FREECAD ASSEMBLY — COMPONENT RECIPES ("Assembly_LinkageUnit")

This assembly document has 6 components, labeled P0..P5 below (a component is one placed body or linked part). 6 of them carry a construction recipe — the FreeCAD feature program that regenerates the part from scratch, quoted from this document or its linked companion documents; the rest are supplied as boundary geometry only. No exploded tour is included for this assembly.
COMPONENT P0 — recipe-attached ("LinkageRod1", a linked part whose construction recipe lives in a companion FreeCAD document of the same project; that document's serialized recipe follows).
Construction recipe (the companion document, serialized — sketch geometry with constraints, then the solid features built on it; lengths are millimeters unless a unit is written):

FCSTD DOCUMENT  (FreeCAD 1.2R45145 (Git))
Label: LinkageRod
License: All rights reserved
LicenseURL: https://en.wikipedia.org/wiki/All_rights_reserved
objects: Sketcher::SketchObject×2, App::Point×1, PartDesign::Pad×1, PartDesign::Chamfer×1, PartDesign::Groove×1, PartDesign::Mirrored×1, PartDesign::Body×1
note: 16 computed .brp shape members not serialized (recipe doc carries the construction recipe); baked Part::Feature solids carry a one-line shape summary decoded from their .brp

FEATURE [App::Point] Origin001
  Role = Origin
FEATURE [Sketcher::SketchObject] Sketch
  ArcFitTolerance = 1e-06
  AttachmentSupport = -> [XZ_Plane]
  ExternalTypes = [0]
  FullyConstrained = true
  MakeInternals = false
  MapMode = 5
  Placement = pos=(0,0,0) rot=(1,0,0;1.5708rad)
  sketch-geometry (1):
    g0: Circle CenterX=0 CenterY=0 CenterZ=0 NormalX=0 NormalY=0 NormalZ=1 AngleXU=0 Radius=1
  constraints (2):
    c: Coincident(g0,g-1)
    c: Diameter(g0) = 2
FEATURE [PartDesign::Pad] Pad
  Direction = (0,-1,2e-16)
  Length = 72
  Length2 = 10
  Placement = pos=(0,0,0) rot=(1,0,0;1.5708rad)
  Profile = -> Sketch
  ReferenceAxis = -> Sketch [N_Axis]
  Refine = true
  SideType = 2
  Suppressed = false
  Type = 0
  Type2 = 0
FEATURE [PartDesign::Chamfer] Chamfer
  Angle = 45
  Base = -> Pad [Edge3,Edge2]
  BaseFeature = -> Pad
  ChamferType = 1
  FlipDirection = false
  Placement = pos=(0,0,0) rot=(1,0,0;1.5708rad)
  Refine = true
  Size = 1
  Size2 = 0.4
  SupportTransform = false
  Suppressed = false
  UseAllEdges = false
FEATURE [Sketcher::SketchObject] Sketch002
  ArcFitTolerance = 1e-06
  AttachmentSupport = -> [Origin]
  ExternalTypes = [0]
  FullyConstrained = true
  MakeInternals = false
  MapMode = 5
  Placement = pos=(0,0,0) rot=(0.57735,0.57735,0.57735;2.0944rad)
  sketch-geometry (2):
    g0: ArcOfCircle CenterX=-36.25 CenterY=0 CenterZ=0 NormalX=0 NormalY=0 NormalZ=1 AngleXU=0 Radius=0.5 StartAngle=0 EndAngle=3.14159
    g1: LineSegment StartX=-36.75 StartY=1e-16 StartZ=0 EndX=-35.75 EndY=1e-16 EndZ=0
  constraints (7):
    c: PointOnObject(g0,g-1)
    c: DistanceX(g0,g-1) = 36.25
    c: Horizontal(g1)
    c: PointOnObject(g1,g-1)
    c: Diameter(g0) = 1
    c: Coincident(g1,g0)
    c: Coincident(g1,g0)
FEATURE [PartDesign::Groove] Groove
  Angle = 360
  Angle2 = 60
  Axis = (1e-16,1,-1e-16)
  Base = (0,0,0)
  BaseFeature = -> Chamfer
  Placement = pos=(0,0,0) rot=(1,0,0;1.5708rad)
  Profile = -> Sketch002
  ReferenceAxis = -> Y_Axis
  Refine = true
  Reversed = true
  Suppressed = false
  Type = 0
FEATURE [PartDesign::Mirrored] Mirrored
  BaseFeature = -> Groove
  MirrorPlane = -> XZ_Plane
  Originals = -> [Groove]
  Placement = pos=(0,0,0) rot=(1,0,0;1.5708rad)
  Refine = true
  Suppressed = false
  TransformMode = 0
FEATURE [PartDesign::Body] Body  label="LinkageRod"
  AllowCompound = false
  Group = -> [Sketch,Pad,Chamfer,Sketch002,Groove,Mirrored]
  Origin = -> Origin
  Tip = -> Mirrored
COMPONENT P1 — same part as P0; its construction recipe is shown at P0.
COMPONENT P2 — recipe-attached ("RubberBandCollet2", a linked part whose construction recipe lives in a companion FreeCAD document of the same project; that document's serialized recipe follows).
Construction recipe (the companion document, serialized — sketch geometry with constraints, then the solid features built on it; lengths are millimeters unless a unit is written):

FCSTD DOCUMENT  (FreeCAD 1.2R45145 (Git))
Label: RubberBandCollet
License: All rights reserved
LicenseURL: https://en.wikipedia.org/wiki/All_rights_reserved
objects: Sketcher::SketchObject×2, App::Point×1, PartDesign::Pad×1, PartDesign::Pocket×1, PartDesign::PolarPattern×1, PartDesign::Chamfer×1, PartDesign::Body×1
note: 16 computed .brp shape members not serialized (recipe doc carries the construction recipe); baked Part::Feature solids carry a one-line shape summary decoded from their .brp

FEATURE [App::Point] Origin001
  Role = Origin
FEATURE [Sketcher::SketchObject] Sketch
  ArcFitTolerance = 1e-06
  AttachmentSupport = -> [Origin]
  ExternalTypes = [0]
  FullyConstrained = true
  MakeInternals = false
  MapMode = 5
  sketch-geometry (8):
    g0: Circle CenterX=0 CenterY=0 CenterZ=0 NormalX=0 NormalY=0 NormalZ=1 AngleXU=0 Radius=1
    g1: ArcOfCircle CenterX=0 CenterY=1 CenterZ=0 NormalX=0 NormalY=0 NormalZ=1 AngleXU=0 Radius=2 StartAngle=2e-16 EndAngle=3.14159
    g2: ArcOfCircle CenterX=0 CenterY=-1 CenterZ=0 NormalX=0 NormalY=0 NormalZ=1 AngleXU=0 Radius=2 StartAngle=3.14159 EndAngle=6.28319
    g3: LineSegment StartX=2 StartY=1 StartZ=0 EndX=2 EndY=-1 EndZ=0
    g4: LineSegment StartX=-2 StartY=1 StartZ=0 EndX=-2 EndY=-1 EndZ=0
    g5: LineSegment [constr] StartX=0 StartY=1 StartZ=0 EndX=0 EndY=-1 EndZ=0
    g6: GeomPoint [constr] X=0 Y=-3 Z=0
    g7: GeomPoint [constr] X=0 Y=3 Z=0
  constraints (17):
    c: Coincident(g0,g-1)
    c: Diameter(g0) = 2
    c: Tangent(g1,g3) = 1.5708
    c: Tangent(g1,g4) = -1.5708
    c: Tangent(g2,g3) = 1.5708
    c: Tangent(g2,g4) = -1.5708
    c: Equal(g1,g2)
    c: Vertical(g4)
    c: Coincident(g5,g1)
    c: Coincident(g5,g2)
    c: Symmetric(g5,g5,g0)
    c: Distance(g3,g4) = 4
    c: PointOnObject(g6,g2)
    c: PointOnObject(g6,g-2)
    c: PointOnObject(g7,g1)
    c: PointOnObject(g7,g-2)
    c: DistanceY(g6,g7) = 6
FEATURE [PartDesign::Pad] Pad
  Direction = (0,0,1)
  Length = 3
  Length2 = 10
  Profile = -> Sketch
  ReferenceAxis = -> Sketch [N_Axis]
  Refine = true
  SideType = 2
  Suppressed = false
  Type = 0
  Type2 = 0
FEATURE [Sketcher::SketchObject] Sketch001
  ArcFitTolerance = 1e-06
  AttachmentSupport = -> [Pad]
  ExternalTypes = [0]
  FullyConstrained = true
  MakeInternals = false
  MapMode = 5
  Placement = pos=(0,0,1.5) rot=(0,0,1;0rad)
  sketch-geometry (5):
    g0: ArcOfCircle CenterX=0 CenterY=2 CenterZ=0 NormalX=0 NormalY=0 NormalZ=1 AngleXU=0 Radius=0.5 StartAngle=2.41886 EndAngle=7.00592
    g1: GeomPoint [constr] X=0 Y=3 Z=0
    g2: LineSegment StartX=-0.375 StartY=2.33072 StartZ=0 EndX=-0.375 EndY=4.33072 EndZ=0
    g3: LineSegment StartX=-0.375 StartY=4.33072 StartZ=0 EndX=0.375 EndY=4.33072 EndZ=0
    g4: LineSegment StartX=0.375 StartY=4.33072 StartZ=0 EndX=0.375 EndY=2.33072 EndZ=0
  constraints (15):
    c: PointOnObject(g0,g-2)
    c: PointOnObject(g1,g-3)
    c: PointOnObject(g1,g-2)
    c: Vertical(g2)
    c: Horizontal(g3)
    c: Vertical(g4)
    c: Horizontal(g4,g2)
    c: Coincident(g2,g3)
    c: Coincident(g3,g4)
    c: DistanceX(g3,g3) = 0.75
    c: Diameter(g0) = 1
    c: Coincident(g2,g0)
    c: Coincident(g4,g0)
    c: DistanceY(g4,g4) = 2
    c: DistanceY(g-1,g0) = 2
FEATURE [PartDesign::Pocket] Pocket
  BaseFeature = -> Pad
  Direction = (0,0,-1)
  Length = 5
  Length2 = 5
  Profile = -> Sketch001
  ReferenceAxis = -> Sketch001 [N_Axis]
  Refine = true
  SideType = 0
  Suppressed = false
  Type = 1
  Type2 = 0
FEATURE [PartDesign::PolarPattern] PolarPattern
  Angle = 360
  Axis = -> Z_Axis
  BaseFeature = -> Pocket
  Mode = 0
  Occurrences = 2
  Offset = 120
  Originals = -> [Pocket]
  Refine = true
  SpacingPattern = [0]
  Spacings = [-1]
  Suppressed = false
  TransformMode = 0
FEATURE [PartDesign::Chamfer] Chamfer
  Angle = 45
  Base = -> PolarPattern [Edge11,Edge25,Edge5,Edge19]
  BaseFeature = -> PolarPattern
  ChamferType = 0
  FlipDirection = false
  Refine = true
  Size = 0.4
  Size2 = 1
  SupportTransform = false
  Suppressed = false
  UseAllEdges = false
FEATURE [PartDesign::Body] Body  label="RubberBandCollet"
  AllowCompound = false
  Group = -> [Sketch,Pad,Sketch001,Pocket,PolarPattern,Chamfer]
  Origin = -> Origin
  Tip = -> Chamfer
COMPONENT P3 — same part as P2; its construction recipe is shown at P2.
COMPONENT P4 — same part as P2; its construction recipe is shown at P2.
COMPONENT P5 — same part as P2; its construction recipe is shown at P2.
PROVENANCE & LICENSES
A FreeCAD (.FCStd) document from a public repository crawl; recipes are the document's own serialized feature recipes (and, for linked parts, companion documents' recipes).
License: other.
